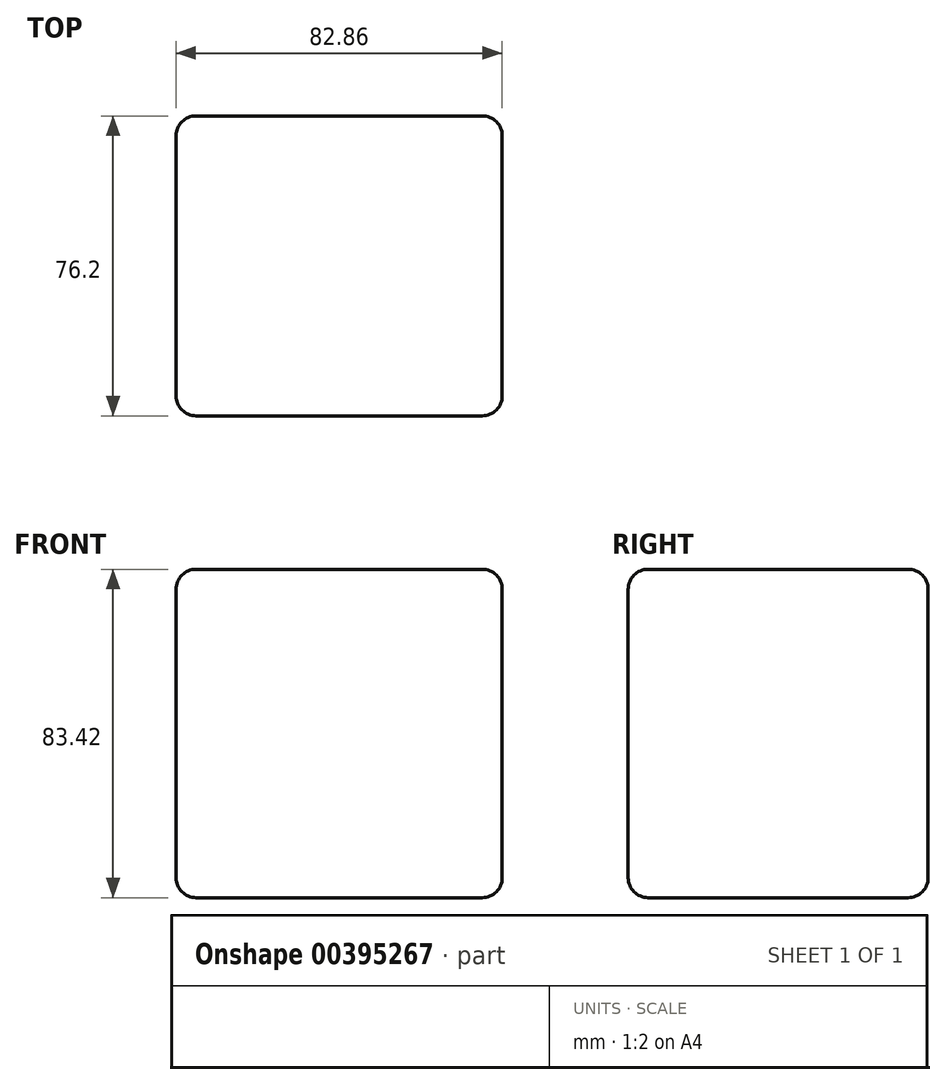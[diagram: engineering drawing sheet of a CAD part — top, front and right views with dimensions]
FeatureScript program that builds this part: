
annotation { "Feature Type Name" : "Feature", "Feature Type Description" : "" }
export const myFeature = defineFeature(function(context is Context, id is Id, definition is map)
    precondition{}
    {
        {
            var Q0;
            Q0=qCreatedBy(makeId("Front.planeOp"),FACE);
            var sketch = newSketch(context, id + "F0", { "sketchPlane" : qUnion([Q0])});
            skLineSegment(sketch, "E0.bottom", {"start": v(-47.55, 44.7) * mm, "end": v(35.3, 44.7) * mm});
            skLineSegment(sketch, "E0.top", {"start": v(-47.55, -38.72) * mm, "end": v(35.3, -38.72) * mm});
            skLineSegment(sketch, "E0.left", {"start": v(-47.55, 44.7) * mm, "end": v(-47.55, -38.72) * mm});
            skLineSegment(sketch, "E0.right", {"start": v(35.3, 44.7) * mm, "end": v(35.3, -38.72) * mm});
            skSolve(sketch);
        }
        {
            var Q0;
            Q0 = qSketchRegion(id + "F0", true);
            extrude(context, id + "F1", {"entities" : qUnion([Q0]), "depth" : 76.2 * mm});
        }
        {
            var Q0;
            Q0=makeQuery(id+"F1.opExtrude","SWEPT_FACE",FACE,{"disambiguationData":[OSD([sQuery(id+"F0.wireOp",EDGE,"E0.left")])]});
            var Q1;
            Q1=makeQuery(id+"F1.opExtrude","SWEPT_FACE",FACE,{"disambiguationData":[OSD([sQuery(id+"F0.wireOp",EDGE,"E0.bottom")])]});
            var Q2;
            Q2=makeQuery(id+"F1.opExtrude","CAP_FACE",FACE,{"disambiguationData":[OSD([sQuery(id+"F0.wireOp",EDGE,"E0.bottom"),sQuery(id+"F0.wireOp",EDGE,"E0.top"),sQuery(id+"F0.wireOp",EDGE,"E0.left"),sQuery(id+"F0.wireOp",EDGE,"E0.right")])],"isStart":false});
            var Q3;
            Q3=makeQuery(id+"F1.opExtrude","SWEPT_FACE",FACE,{"disambiguationData":[OSD([sQuery(id+"F0.wireOp",EDGE,"E0.top")])]});
            var Q4;
            Q4=makeQuery(id+"F1.opExtrude","SWEPT_FACE",FACE,{"disambiguationData":[OSD([sQuery(id+"F0.wireOp",EDGE,"E0.right")])]});
            fillet(context, id + "F2", {"entities" : qUnion([Q0, Q1, Q2, Q3, Q4]), "radius" : 5.08 * mm, "tangentPropagation" : true, "allowEdgeOverflow" : false});
        }
    });
